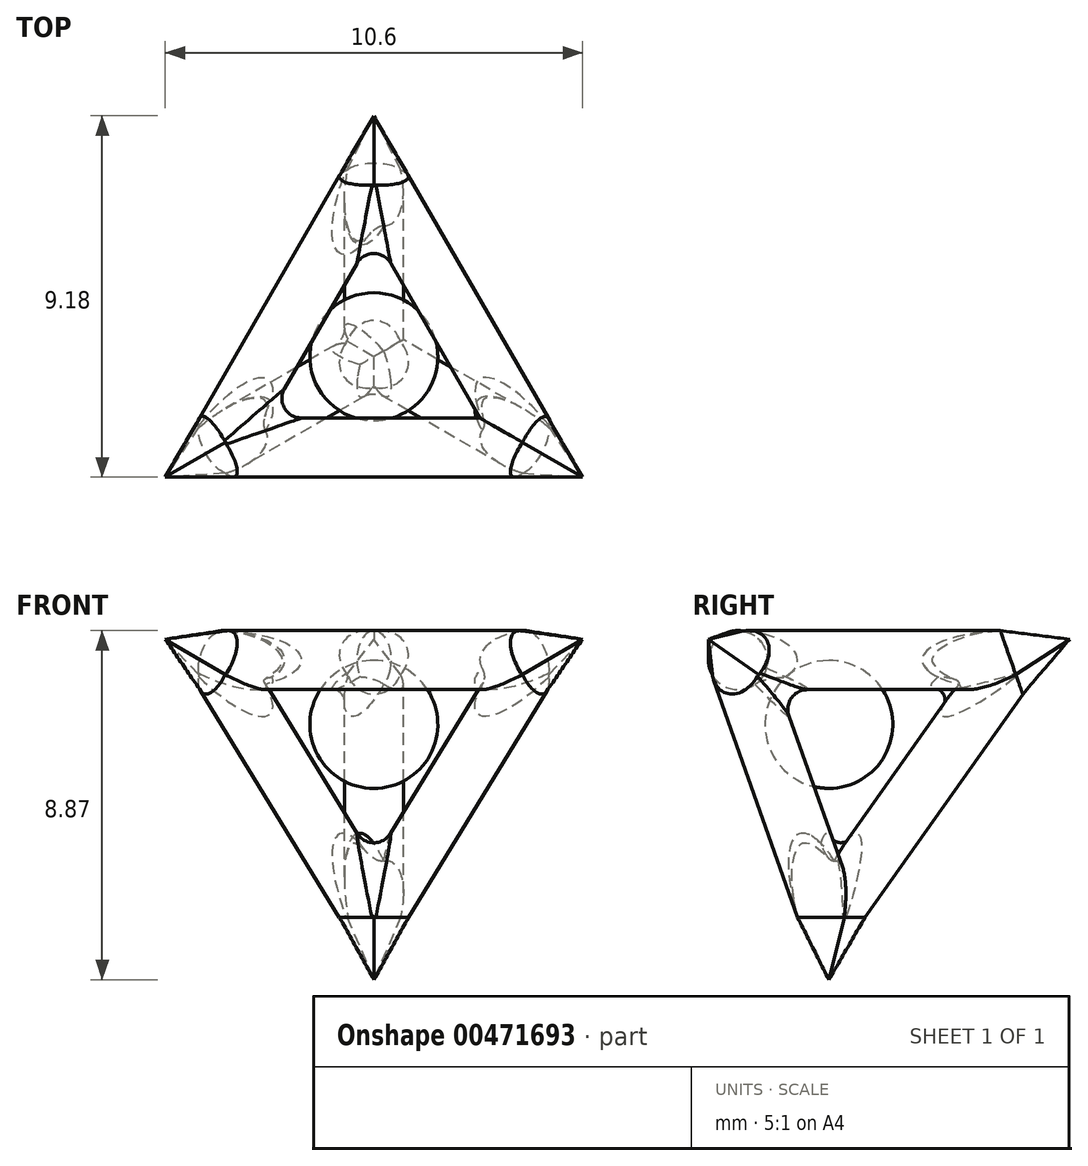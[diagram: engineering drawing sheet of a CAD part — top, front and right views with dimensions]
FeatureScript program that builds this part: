
annotation { "Feature Type Name" : "Feature", "Feature Type Description" : "" }
export const myFeature = defineFeature(function(context is Context, id is Id, definition is map)
    precondition{}
    {
        {
            assignVariable(context, id + "F0", {"name" : "offset", "anyValue" : 1.59});
        }
        {
            var Q0;
            Q0=qCreatedBy(makeId("Top.planeOp"),FACE);
            var sketch = newSketch(context, id + "F1", { "sketchPlane" : qUnion([Q0])});
            skLineSegment(sketch, "E0", {"start": v(0, 4.62) * mm, "end": v(-4, -2.3) * mm});
            skLineSegment(sketch, "E1", {"start": v(-4, -2.3) * mm, "end": v(4, -2.3) * mm});
            skLineSegment(sketch, "E2", {"start": v(4, -2.3) * mm, "end": v(0, 4.62) * mm});
            skLineSegment(sketch, "E3", {"start": v(0, 0) * mm, "end": v(0, 4.62) * mm, "construction": true});
            skLineSegment(sketch, "E4", {"start": v(4, -2.3) * mm, "end": v(0, 0) * mm, "construction": true});
            skLineSegment(sketch, "E5", {"start": v(-4, -2.3) * mm, "end": v(0, 0) * mm, "construction": true});
            skSolve(sketch);
        }
        {
            var Q0;
            Q0=qCreatedBy(makeId("Right.planeOp"),FACE);
            var sketch = newSketch(context, id + "F2", { "sketchPlane" : qUnion([Q0])});
            skCircle(sketch, "E6", {"center": v(-2.3, 0) * mm, "radius": 0.75 * mm});
            skSolve(sketch);
        }
        {
            var Q0;
            Q0=makeQuery(id+"F2.imprint","IMPRINT",FACE,{"disambiguationData":[TD([[makeQuery(id+"F2.imprint","IMPRINT",EDGE,{"derivedFrom":sQuery(id+"F2.wireOp",EDGE,"E6")}),1.0]])]});
            var Q1;
            Q1=sQuery(id+"F1.wireOp",EDGE,"E1");
            var Q2;
            Q2=sQuery(id+"F1.wireOp",EDGE,"E0");
            var Q3;
            Q3=sQuery(id+"F1.wireOp",EDGE,"E2");
            sweep(context, id + "F3", {"profiles" : qUnion([Q0]), "path" : qUnion([Q1, Q2, Q3])});
        }
        {
            var Q0;
            Q0=qCreatedBy(makeId("Right.planeOp"),FACE);
            var sketch = newSketch(context, id + "F4", { "sketchPlane" : qUnion([Q0])});
            skLineSegment(sketch, "E7", {"start": v(4.62, 0) * mm, "end": v(0, -6.53) * mm});
            skLineSegment(sketch, "E8", {"start": v(0, -6.53) * mm, "end": v(0, 0) * mm, "construction": true});
            skSolve(sketch);
        }
        {
            var Q0;
            Q0=sQuery(id+"F4.wireOp",VERTEX,"E8.start");
            var Q1;
            Q1=sQuery(id+"F1.wireOp",VERTEX,"E3.end");
            var Q2;
            Q2=sQuery(id+"F1.wireOp",VERTEX,"E5.start");
            cPlane(context, id + "F5", {"entities" : qUnion([Q0, Q1, Q2]), "cplaneType" : CPlaneType.THREE_POINT, "offset" : 25 * mm, "width" : 150 * mm, "height" : 150 * mm});
        }
        {
            var Q0;
            Q0=qCreatedBy(id+"F5.planeOp",FACE);
            var sketch = newSketch(context, id + "F6", { "sketchPlane" : qUnion([Q0])});
            skLineSegment(sketch, "E9", {"start": v(1.16, -6.05) * mm, "end": v(3.78, 1.51) * mm});
            skLineSegment(sketch, "E10", {"start": v(3.78, 1.51) * mm, "end": v(-4.07, 0) * mm});
            skLineSegment(sketch, "E11", {"start": v(-4.07, 0) * mm, "end": v(1.16, -6.05) * mm});
            skSolve(sketch);
        }
        {
            var Q0;
            Q0=sQuery(id+"F4.wireOp",VERTEX,"E8.start");
            var Q1;
            Q1=sQuery(id+"F1.wireOp",VERTEX,"E2.start");
            var Q2;
            Q2=sQuery(id+"F1.wireOp",VERTEX,"E3.end");
            cPlane(context, id + "F7", {"entities" : qUnion([Q0, Q1, Q2]), "cplaneType" : CPlaneType.THREE_POINT, "offset" : 25 * mm, "width" : 150 * mm, "height" : 150 * mm});
        }
        {
            var Q0;
            Q0=sQuery(id+"F4.wireOp",VERTEX,"E8.start");
            var Q1;
            Q1=sQuery(id+"F1.wireOp",VERTEX,"E4.start");
            var Q2;
            Q2=sQuery(id+"F1.wireOp",VERTEX,"E1.start");
            cPlane(context, id + "F8", {"entities" : qUnion([Q0, Q1, Q2]), "cplaneType" : CPlaneType.THREE_POINT, "offset" : 25 * mm, "width" : 150 * mm, "height" : 150 * mm});
        }
        {
            var Q0;
            Q0=qCreatedBy(id+"F7.planeOp",FACE);
            var sketch = newSketch(context, id + "F9", { "sketchPlane" : qUnion([Q0])});
            skLineSegment(sketch, "E12", {"start": v(-1.16, -6.05) * mm, "end": v(4.07, 0) * mm});
            skLineSegment(sketch, "E13", {"start": v(4.07, 0) * mm, "end": v(-3.78, 1.51) * mm});
            skLineSegment(sketch, "E14", {"start": v(-3.78, 1.51) * mm, "end": v(-1.16, -6.05) * mm});
            skSolve(sketch);
        }
        {
            var Q0;
            Q0 = qSketchRegion(id + "F2", true);
            var Q1;
            Q1=sQuery(id+"F1.wireOp",EDGE,"E1");
            var Q2;
            Q2=sQuery(id+"F9.wireOp",EDGE,"E14");
            var Q3;
            Q3=sQuery(id+"F6.wireOp",EDGE,"E9");
            sweep(context, id + "F10", {"operationType" : NewBodyOperationType.ADD, "profiles" : qUnion([Q0]), "path" : qUnion([Q1, Q2, Q3])});
        }
        {
            var Q0;
            Q0=sQuery(id+"F1.wireOp",VERTEX,"E5.end");
            var Q1;
            Q1=sQuery(id+"F4.wireOp",VERTEX,"E8.start");
            var Q2;
            Q2=sQuery(id+"F1.wireOp",VERTEX,"E1.start");
            cPlane(context, id + "F11", {"entities" : qUnion([Q0, Q1, Q2]), "cplaneType" : CPlaneType.THREE_POINT, "offset" : 25 * mm, "width" : 150 * mm, "height" : 150 * mm});
        }
        {
            var Q0;
            Q0=qCreatedBy(id+"F11.planeOp",FACE);
            var sketch = newSketch(context, id + "F12", { "sketchPlane" : qUnion([Q0])});
            skCircle(sketch, "E15", {"center": v(2.3, 0) * mm, "radius": 0.75 * mm});
            skSolve(sketch);
        }
        {
            var Q0;
            Q0 = qSketchRegion(id + "F12", true);
            var Q1;
            Q1=sQuery(id+"F1.wireOp",EDGE,"E2");
            var Q2;
            Q2=sQuery(id+"F4.wireOp",EDGE,"E7");
            var Q3;
            Q3=sQuery(id+"F9.wireOp",EDGE,"E14");
            sweep(context, id + "F13", {"operationType" : NewBodyOperationType.ADD, "profiles" : qUnion([Q0]), "path" : qUnion([Q1, Q2, Q3])});
        }
        {
            var Q0;
            Q0=qCreatedBy(id+"F5.planeOp",FACE);
            var sketch = newSketch(context, id + "F14", { "sketchPlane" : qUnion([Q0])});
            skLineSegment(sketch, "E16", {"start": v(3.78, 1.51) * mm, "end": v(0.3, -1.51) * mm});
            skLineSegment(sketch, "E17", {"start": v(0.3, -1.51) * mm, "end": v(-4.07, 0) * mm});
            skLineSegment(sketch, "E18", {"start": v(0.3, -1.51) * mm, "end": v(1.16, -6.05) * mm});
            skSolve(sketch);
        }
        {
            var Q0;
            Q0=sQuery(id+"F14.wireOp",VERTEX,"E18.end");
            var Q1;
            Q1=sQuery(id+"F4.wireOp",EDGE,"E8");
            cPlane(context, id + "F15", {"entities" : qUnion([Q0, Q1]), "cplaneType" : CPlaneType.LINE_POINT, "offset" : 25 * mm, "width" : 150 * mm, "height" : 150 * mm});
        }
        {
            var Q0;
            Q0=qCreatedBy(id+"F15.planeOp",FACE);
            var sketch = newSketch(context, id + "F16", { "sketchPlane" : qUnion([Q0])});
            skCircle(sketch, "E19", {"center": v(0, 0) * mm, "radius": 1.25 * mm});
            skSolve(sketch);
        }
        {
            var Q0;
            Q0=makeQuery(id+"F16.imprint","IMPRINT",FACE,{"disambiguationData":[TD([[makeQuery(id+"F16.imprint","IMPRINT",EDGE,{"derivedFrom":sQuery(id+"F16.wireOp",EDGE,"E19")}),1.0]])]});
            extrude(context, id + "F17", {"entities" : qUnion([Q0]), "operationType" : NewBodyOperationType.REMOVE, "endBound" : BoundingType.THROUGH_ALL, "oppositeDirection" : true, "depth" : 25 * mm});
        }
        {
            var Q0;
            Q0=makeQuery(id+"F17.boolean.opBoolean","COPY",FACE,{"derivedFrom":makeQuery(id+"F17.opExtrude","CAP_FACE",FACE,{"disambiguationData":[OSD([sQuery(id+"F16.wireOp",EDGE,"E19")])],"isStart":true})});
            cPlane(context, id + "F18", {"entities" : qUnion([Q0]), "cplaneType" : CPlaneType.OFFSET, "offset" : getVariable(context, 'offset') * mm, "width" : 150 * mm, "height" : 150 * mm});
        }
        {
            var Q0;
            Q0=qCreatedBy(id+"F18.planeOp",FACE);
            var sketch = newSketch(context, id + "F19", { "sketchPlane" : qUnion([Q0])});
            skPoint(sketch, "E20", {"position": v(0, 0) * mm});
            skSolve(sketch);
        }
        {
            var Q1;
            Q1=makeQuery(id+"F17.boolean.opBoolean","COPY",FACE,{"derivedFrom":makeQuery(id+"F17.opExtrude","CAP_FACE",FACE,{"disambiguationData":[OSD([sQuery(id+"F16.wireOp",EDGE,"E19")])],"isStart":true})});
            var Q2;
            Q2=sQuery(id+"F19.wireOp",VERTEX,"E20");
            loft(context, id + "F20", {"operationType" : NewBodyOperationType.ADD, "sheetProfilesArray" : [{ "sheetProfileEntities" : qUnion([Q1]) }, { "sheetProfileEntities" : qUnion([Q2]) }]});
        }
        {
            var Q0;
            Q0=sQuery(id+"F14.wireOp",VERTEX,"E16.end");
            var Q1;
            Q1=sQuery(id+"F14.wireOp",VERTEX,"E18.end");
            var Q2;
            Q2=sQuery(id+"F1.wireOp",VERTEX,"E4.start");
            cPlane(context, id + "F21", {"entities" : qUnion([Q0, Q1, Q2]), "cplaneType" : CPlaneType.THREE_POINT, "offset" : 25 * mm, "width" : 150 * mm, "height" : 150 * mm});
        }
        {
            var Q0;
            Q0=qCreatedBy(id+"F21.planeOp",FACE);
            var sketch = newSketch(context, id + "F22", { "sketchPlane" : qUnion([Q0])});
            skLineSegment(sketch, "E21", {"start": v(1.54, -2.18) * mm, "end": v(-4.62, 0) * mm});
            skSolve(sketch);
        }
        {
            var Q0;
            Q0=sQuery(id+"F22.wireOp",VERTEX,"E21.end");
            var Q1;
            Q1=sQuery(id+"F22.wireOp",EDGE,"E21");
            cPlane(context, id + "F23", {"entities" : qUnion([Q0, Q1]), "cplaneType" : CPlaneType.LINE_POINT, "offset" : 25 * mm, "width" : 150 * mm, "height" : 150 * mm});
        }
        {
            var Q0;
            Q0=qCreatedBy(id+"F23.planeOp",FACE);
            var sketch = newSketch(context, id + "F24", { "sketchPlane" : qUnion([Q0])});
            skCircle(sketch, "E22", {"center": v(-0.3, -1.51) * mm, "radius": 1.25 * mm});
            skSolve(sketch);
        }
        {
            var Q0;
            Q0 = qSketchRegion(id + "F24", true);
            extrude(context, id + "F25", {"entities" : qUnion([Q0]), "operationType" : NewBodyOperationType.REMOVE, "endBound" : BoundingType.THROUGH_ALL, "depth" : 25 * mm});
        }
        {
            var Q0;
            Q0=makeQuery(id+"F25.boolean.opBoolean","COPY",FACE,{"derivedFrom":makeQuery(id+"F25.opExtrude","CAP_FACE",FACE,{"disambiguationData":[OSD([sQuery(id+"F24.wireOp",EDGE,"E22")])],"isStart":true})});
            cPlane(context, id + "F26", {"entities" : qUnion([Q0]), "cplaneType" : CPlaneType.OFFSET, "offset" : getVariable(context, 'offset') * mm, "width" : 150 * mm, "height" : 150 * mm});
        }
        {
            var Q0;
            Q0=qCreatedBy(id+"F26.planeOp",FACE);
            var sketch = newSketch(context, id + "F27", { "sketchPlane" : qUnion([Q0])});
            skPoint(sketch, "E23", {"position": v(-0.3, -1.51) * mm});
            skSolve(sketch);
        }
        {
            var Q0;
            Q0=makeQuery(id+"F25.boolean.opBoolean","COPY",FACE,{"derivedFrom":makeQuery(id+"F25.opExtrude","CAP_FACE",FACE,{"disambiguationData":[OSD([sQuery(id+"F24.wireOp",EDGE,"E22")])],"isStart":true})});
            var Q1;
            Q1=sQuery(id+"F27.wireOp",VERTEX,"E23");
            loft(context, id + "F28", {"operationType" : NewBodyOperationType.ADD, "sheetProfilesArray" : [{ "sheetProfileEntities" : qUnion([Q0]) }, { "sheetProfileEntities" : qUnion([Q1]) }]});
        }
        {
            var Q0;
            Q0=qCreatedBy(id+"F7.planeOp",FACE);
            var sketch = newSketch(context, id + "F29", { "sketchPlane" : qUnion([Q0])});
            skLineSegment(sketch, "E24", {"start": v(4.07, 0) * mm, "end": v(-0.3, -1.51) * mm});
            skLineSegment(sketch, "E25", {"start": v(-0.3, -1.51) * mm, "end": v(-1.16, -6.05) * mm});
            skLineSegment(sketch, "E26", {"start": v(-0.3, -1.51) * mm, "end": v(-3.78, 1.51) * mm});
            skSolve(sketch);
        }
        {
            var Q0;
            Q0=sQuery(id+"F29.wireOp",VERTEX,"E25.start");
            var Q1;
            Q1=sQuery(id+"F29.wireOp",VERTEX,"E26.end");
            var Q2;
            Q2=sQuery(id+"F6.wireOp",VERTEX,"E10.start");
            cPlane(context, id + "F30", {"entities" : qUnion([Q0, Q1, Q2]), "cplaneType" : CPlaneType.THREE_POINT, "offset" : 25 * mm, "width" : 150 * mm, "height" : 150 * mm});
        }
        {
            var Q0;
            Q0=qCreatedBy(id+"F30.planeOp",FACE);
            var sketch = newSketch(context, id + "F31", { "sketchPlane" : qUnion([Q0])});
            skLineSegment(sketch, "E27", {"start": v(-4, -1.89) * mm, "end": v(1.33, 1.89) * mm});
            skSolve(sketch);
        }
        {
            var Q0;
            Q0=sQuery(id+"F31.wireOp",VERTEX,"E27.start");
            var Q1;
            Q1=sQuery(id+"F31.wireOp",EDGE,"E27");
            cPlane(context, id + "F32", {"entities" : qUnion([Q0, Q1]), "cplaneType" : CPlaneType.LINE_POINT, "offset" : 25 * mm, "width" : 150 * mm, "height" : 150 * mm});
        }
        {
            var Q0;
            Q0=qCreatedBy(id+"F32.planeOp",FACE);
            var sketch = newSketch(context, id + "F33", { "sketchPlane" : qUnion([Q0])});
            skCircle(sketch, "E28", {"center": v(-0.3, -1.51) * mm, "radius": 1.25 * mm});
            skSolve(sketch);
        }
        {
            var Q0;
            Q0 = qSketchRegion(id + "F33", true);
            extrude(context, id + "F34", {"entities" : qUnion([Q0]), "operationType" : NewBodyOperationType.REMOVE, "endBound" : BoundingType.THROUGH_ALL, "oppositeDirection" : true, "depth" : 25 * mm});
        }
        {
            var Q0;
            Q0=makeQuery(id+"F34.boolean.opBoolean","COPY",FACE,{"derivedFrom":makeQuery(id+"F34.opExtrude","CAP_FACE",FACE,{"disambiguationData":[OSD([sQuery(id+"F33.wireOp",EDGE,"E28")])],"isStart":true})});
            cPlane(context, id + "F35", {"entities" : qUnion([Q0]), "cplaneType" : CPlaneType.OFFSET, "offset" : getVariable(context, 'offset') * mm, "width" : 150 * mm, "height" : 150 * mm});
        }
        {
            var Q0;
            Q0=qCreatedBy(id+"F35.planeOp",FACE);
            var sketch = newSketch(context, id + "F36", { "sketchPlane" : qUnion([Q0])});
            skPoint(sketch, "E29", {"position": v(0.3, -1.51) * mm});
            skSolve(sketch);
        }
        {
            var Q0;
            Q0=makeQuery(id+"F34.boolean.opBoolean","COPY",FACE,{"derivedFrom":makeQuery(id+"F34.opExtrude","CAP_FACE",FACE,{"disambiguationData":[OSD([sQuery(id+"F33.wireOp",EDGE,"E28")])],"isStart":true})});
            var Q1;
            Q1=sQuery(id+"F36.wireOp",VERTEX,"E29");
            loft(context, id + "F37", {"operationType" : NewBodyOperationType.ADD, "sheetProfilesArray" : [{ "sheetProfileEntities" : qUnion([Q0]) }, { "sheetProfileEntities" : qUnion([Q1]) }]});
        }
        {
            var Q0;
            Q0=qCreatedBy(id+"F8.planeOp",FACE);
            var sketch = newSketch(context, id + "F38", { "sketchPlane" : qUnion([Q0])});
            skLineSegment(sketch, "E30", {"start": v(-4, 0.77) * mm, "end": v(0, -1.54) * mm});
            skLineSegment(sketch, "E31", {"start": v(0, -1.54) * mm, "end": v(0, -6.16) * mm});
            skLineSegment(sketch, "E32", {"start": v(0, -1.54) * mm, "end": v(4, 0.77) * mm});
            skSolve(sketch);
        }
        {
            var Q0;
            Q0=sQuery(id+"F38.wireOp",VERTEX,"E31.start");
            var Q1;
            Q1=sQuery(id+"F38.wireOp",VERTEX,"E32.end");
            var Q2;
            Q2=sQuery(id+"F29.wireOp",VERTEX,"E24.start");
            cPlane(context, id + "F39", {"entities" : qUnion([Q0, Q1, Q2]), "cplaneType" : CPlaneType.THREE_POINT, "offset" : 25 * mm, "width" : 150 * mm, "height" : 150 * mm});
        }
        {
            var Q0;
            Q0=qCreatedBy(id+"F39.planeOp",FACE);
            var sketch = newSketch(context, id + "F40", { "sketchPlane" : qUnion([Q0])});
            skLineSegment(sketch, "E33", {"start": v(0.77, 4.35) * mm, "end": v(0.77, -2.18) * mm});
            skSolve(sketch);
        }
        {
            var Q0;
            Q0=sQuery(id+"F40.wireOp",VERTEX,"E33.start");
            var Q1;
            Q1=sQuery(id+"F40.wireOp",EDGE,"E33");
            cPlane(context, id + "F41", {"entities" : qUnion([Q0, Q1]), "cplaneType" : CPlaneType.LINE_POINT, "offset" : 25 * mm, "width" : 150 * mm, "height" : 150 * mm});
        }
        {
            var Q0;
            Q0=qCreatedBy(id+"F41.planeOp",FACE);
            var sketch = newSketch(context, id + "F42", { "sketchPlane" : qUnion([Q0])});
            skCircle(sketch, "E34", {"center": v(0, -1.54) * mm, "radius": 1.25 * mm});
            skSolve(sketch);
        }
        {
            var Q0;
            Q0=makeQuery(id+"F42.imprint","IMPRINT",FACE,{"disambiguationData":[TD([[makeQuery(id+"F42.imprint","IMPRINT",EDGE,{"derivedFrom":sQuery(id+"F42.wireOp",EDGE,"E34")}),1.0]])]});
            extrude(context, id + "F43", {"entities" : qUnion([Q0]), "operationType" : NewBodyOperationType.REMOVE, "endBound" : BoundingType.THROUGH_ALL, "oppositeDirection" : true, "depth" : 25 * mm});
        }
        {
            var Q0;
            Q0=makeQuery(id+"F43.boolean.opBoolean","COPY",FACE,{"derivedFrom":makeQuery(id+"F43.opExtrude","CAP_FACE",FACE,{"disambiguationData":[OSD([sQuery(id+"F42.wireOp",EDGE,"E34")])],"isStart":true})});
            cPlane(context, id + "F44", {"entities" : qUnion([Q0]), "cplaneType" : CPlaneType.OFFSET, "offset" : getVariable(context, 'offset') * mm, "width" : 150 * mm, "height" : 150 * mm});
        }
        {
            var Q0;
            Q0=qCreatedBy(id+"F44.planeOp",FACE);
            var sketch = newSketch(context, id + "F45", { "sketchPlane" : qUnion([Q0])});
            skPoint(sketch, "E35", {"position": v(0, -1.54) * mm});
            skSolve(sketch);
        }
        {
            var Q0;
            Q0=makeQuery(id+"F43.boolean.opBoolean","COPY",FACE,{"derivedFrom":makeQuery(id+"F43.opExtrude","CAP_FACE",FACE,{"disambiguationData":[OSD([sQuery(id+"F42.wireOp",EDGE,"E34")])],"isStart":true})});
            var Q1;
            Q1=sQuery(id+"F45.wireOp",VERTEX,"E35");
            loft(context, id + "F46", {"operationType" : NewBodyOperationType.ADD, "sheetProfilesArray" : [{ "sheetProfileEntities" : qUnion([Q0]) }, { "sheetProfileEntities" : qUnion([Q1]) }]});
        }
        {
            var Q0;
            {var subQ0=sQuery(id+"F2.wireOp",EDGE,"E6");Q0=makeQuery(id+"F10.boolean.opBoolean","INTERSECT",EDGE,{"disambiguationData":[OD(3.0)],"derivedFrom":[makeQuery(id+"F3.opSweep","SWEPT_FACE",FACE,{"disambiguationData":[OSD([sQuery(id+"F1.wireOp",EDGE,"E0"),subQ0])]}),makeQuery(id+"F10.opSweep","SWEPT_FACE",FACE,{"disambiguationData":[OSD([subQ0,sQuery(id+"F6.wireOp",EDGE,"E9")])]})]});}
            var Q1;
            Q1=makeQuery(id+"F10.boolean.opBoolean","SPLIT",EDGE,{"disambiguationData":[OD(1.0)],"derivedFrom":makeQuery(id+"F10.opSweep","MID_CAP_EDGE",EDGE,{"disambiguationData":[OSD([sQuery(id+"F2.wireOp",EDGE,"E6"),sQuery(id+"F6.wireOp",VERTEX,"E9.end")])],"capPos":1.0})});
            var Q2;
            Q2=makeQuery(id+"F10.boolean.opBoolean","SPLIT",EDGE,{"disambiguationData":[OD(1.0)],"derivedFrom":makeQuery(id+"F3.opSweep","MID_CAP_EDGE",EDGE,{"disambiguationData":[OSD([sQuery(id+"F1.wireOp",VERTEX,"E0.end"),sQuery(id+"F2.wireOp",EDGE,"E6")])],"capPos":1.0})});
            var Q3;
            Q3=makeQuery(id+"F13.boolean.opBoolean","SPLIT",EDGE,{"disambiguationData":[OD(1.0)],"derivedFrom":makeQuery(id+"F3.opSweep","MID_CAP_EDGE",EDGE,{"disambiguationData":[OSD([sQuery(id+"F1.wireOp",VERTEX,"E2.end"),sQuery(id+"F2.wireOp",EDGE,"E6")])],"capPos":2.0})});
            var Q4;
            {var subQ0=sQuery(id+"F2.wireOp",EDGE,"E6");var subQ1=sQuery(id+"F1.wireOp",EDGE,"E1");var subQ2=makeQuery(id+"F3.opSweep","SWEPT_FACE",FACE,{"disambiguationData":[OSD([sQuery(id+"F1.wireOp",EDGE,"E0"),subQ0])]});Q4=makeQuery(id+"F13.boolean.opBoolean","INTERSECT",EDGE,{"disambiguationData":[OD(3.0)],"derivedFrom":[makeQuery(id+"F10.boolean.opBoolean","SPLIT",FACE,{"disambiguationData":[TD([subQ2,makeQuery(id+"F3.opSweep","SWEPT_FACE",FACE,{"disambiguationData":[OSD([subQ1,subQ0])]}),makeQuery(id+"F3.opSweep","SWEPT_FACE",FACE,{"disambiguationData":[OSD([sQuery(id+"F1.wireOp",EDGE,"E2"),subQ0])]}),makeQuery(id+"F10.opSweep","SWEPT_FACE",FACE,{"disambiguationData":[OSD([subQ1,subQ0])]}),makeQuery(id+"F10.opSweep","SWEPT_FACE",FACE,{"disambiguationData":[OSD([subQ0,sQuery(id+"F6.wireOp",EDGE,"E9")])]})])],"derivedFrom":subQ2}),makeQuery(id+"F13.opSweep","SWEPT_FACE",FACE,{"disambiguationData":[OSD([sQuery(id+"F4.wireOp",EDGE,"E7"),sQuery(id+"F12.wireOp",EDGE,"E15")])]})]});}
            var Q5;
            Q5=makeQuery(id+"F13.boolean.opBoolean","SPLIT",EDGE,{"disambiguationData":[OD(1.0)],"derivedFrom":makeQuery(id+"F13.opSweep","MID_CAP_EDGE",EDGE,{"disambiguationData":[OSD([sQuery(id+"F4.wireOp",VERTEX,"E7.start"),sQuery(id+"F12.wireOp",EDGE,"E15")])],"capPos":1.0})});
            var Q6;
            Q6=makeQuery(id+"F13.boolean.opBoolean","SPLIT",EDGE,{"disambiguationData":[OD(1.0)],"derivedFrom":makeQuery(id+"F10.opSweep","MID_CAP_EDGE",EDGE,{"disambiguationData":[OSD([sQuery(id+"F2.wireOp",EDGE,"E6"),sQuery(id+"F6.wireOp",VERTEX,"E9.start")])],"capPos":2.0})});
            var Q7;
            {var subQ0=sQuery(id+"F2.wireOp",EDGE,"E6");var subQ1=sQuery(id+"F1.wireOp",EDGE,"E1");var subQ2=makeQuery(id+"F10.opSweep","SWEPT_FACE",FACE,{"disambiguationData":[OSD([subQ0,sQuery(id+"F6.wireOp",EDGE,"E9")])]});Q7=makeQuery(id+"F13.boolean.opBoolean","INTERSECT",EDGE,{"disambiguationData":[OD(3.0)],"derivedFrom":[makeQuery(id+"F10.boolean.opBoolean","SPLIT",FACE,{"disambiguationData":[TD([makeQuery(id+"F3.opSweep","SWEPT_FACE",FACE,{"disambiguationData":[OSD([sQuery(id+"F1.wireOp",EDGE,"E0"),subQ0])]}),makeQuery(id+"F3.opSweep","SWEPT_FACE",FACE,{"disambiguationData":[OSD([subQ1,subQ0])]}),makeQuery(id+"F10.opSweep","SWEPT_FACE",FACE,{"disambiguationData":[OSD([subQ1,subQ0])]}),subQ2,makeQuery(id+"F10.opSweep","SWEPT_FACE",FACE,{"disambiguationData":[OSD([subQ0,sQuery(id+"F9.wireOp",EDGE,"E14")])]})])],"derivedFrom":subQ2}),makeQuery(id+"F13.opSweep","SWEPT_FACE",FACE,{"disambiguationData":[OSD([sQuery(id+"F4.wireOp",EDGE,"E7"),sQuery(id+"F12.wireOp",EDGE,"E15")])]})]});}
            var Q8;
            Q8=makeQuery(id+"F13.boolean.opBoolean","SPLIT",EDGE,{"disambiguationData":[OD(1.0)],"derivedFrom":makeQuery(id+"F13.opSweep","MID_CAP_EDGE",EDGE,{"disambiguationData":[OSD([sQuery(id+"F9.wireOp",VERTEX,"E14.end"),sQuery(id+"F12.wireOp",EDGE,"E15")])],"capPos":2.0})});
            var Q9;
            Q9=makeQuery(id+"F10.boolean.opBoolean","SPLIT",EDGE,{"disambiguationData":[OD(1.0)],"derivedFrom":makeQuery(id+"F3.opSweep","CAP_EDGE",EDGE,{"disambiguationData":[OSD([sQuery(id+"F1.wireOp",VERTEX,"E2.start"),sQuery(id+"F2.wireOp",EDGE,"E6")])],"isStart":true})});
            var Q10;
            Q10=makeQuery(id+"F10.boolean.opBoolean","SPLIT",EDGE,{"disambiguationData":[OD(1.0)],"derivedFrom":makeQuery(id+"F10.opSweep","CAP_EDGE",EDGE,{"disambiguationData":[OSD([sQuery(id+"F2.wireOp",EDGE,"E6"),sQuery(id+"F9.wireOp",VERTEX,"E14.start")])],"isStart":true})});
            var Q11;
            {var subQ0=sQuery(id+"F2.wireOp",EDGE,"E6");Q11=makeQuery(id+"F10.boolean.opBoolean","INTERSECT",EDGE,{"disambiguationData":[OD(3.0)],"derivedFrom":[makeQuery(id+"F3.opSweep","SWEPT_FACE",FACE,{"disambiguationData":[OSD([sQuery(id+"F1.wireOp",EDGE,"E2"),subQ0])]}),makeQuery(id+"F10.opSweep","SWEPT_FACE",FACE,{"disambiguationData":[OSD([subQ0,sQuery(id+"F9.wireOp",EDGE,"E14")])]})]});}
            fillet(context, id + "F47", {"entities" : qUnion([Q0, Q1, Q2, Q3, Q4, Q5, Q6, Q7, Q8, Q9, Q10, Q11]), "radius" : 0.5 * mm, "tangentPropagation" : true, "allowEdgeOverflow" : false});
        }
        {
            var Q0;
            Q0=qCreatedBy(makeId("Front.planeOp"),FACE);
            var sketch = newSketch(context, id + "F48", { "sketchPlane" : qUnion([Q0])});
            skArc(sketch, "E36", {"start": v(0, -3.26) * mm, "mid": v(1.62, -1.63) * mm, "end": v(0, 0) * mm});
            skLineSegment(sketch, "E37", {"start": v(0, -3.26) * mm, "end": v(0, 0) * mm});
            skSolve(sketch);
        }
        {
            var Q0;
            Q0 = qSketchRegion(id + "F48", true);
            var Q1;
            Q1=sQuery(id+"F48.wireOp",EDGE,"E37");
            revolve(context, id + "F49", {"entities" : qUnion([Q0]), "axis" : qUnion([Q1]), "revolveType" : RevolveType.FULL});
        }
    });
